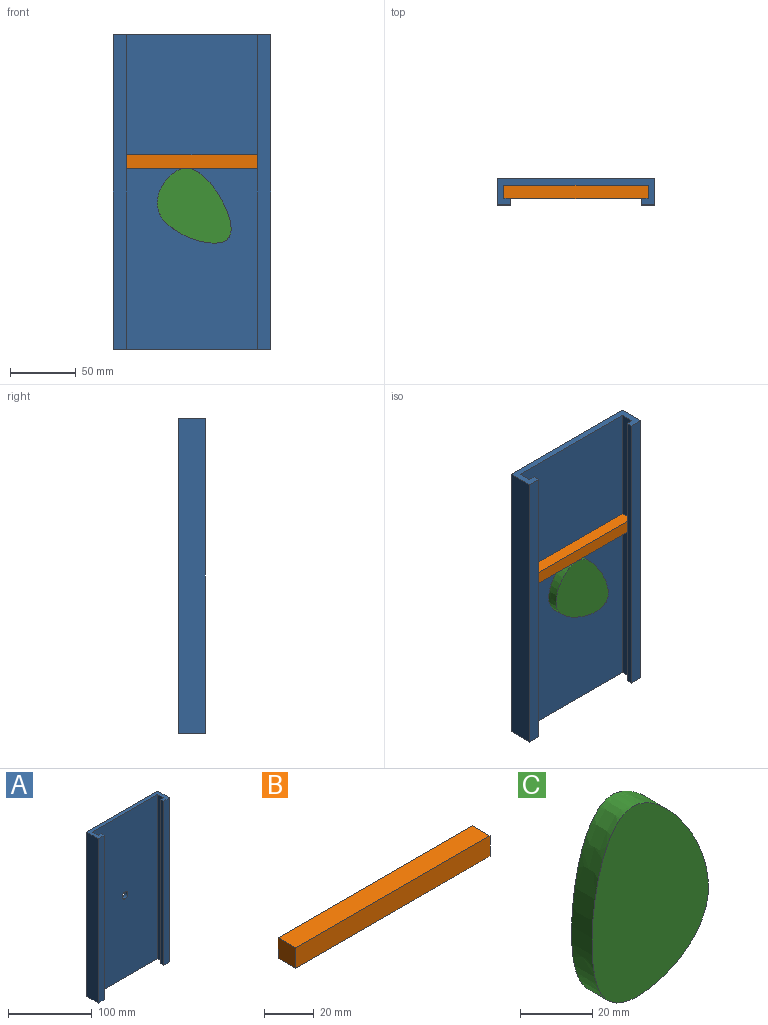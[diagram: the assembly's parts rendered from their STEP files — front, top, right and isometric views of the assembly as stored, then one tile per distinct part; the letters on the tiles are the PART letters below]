
ASSEMBLY  parts=3 mates=2
PART A: 15 faces, bbox 120x20x240 mm
  f0: plane 240x5mm, normal (1,0,0), area 1200mm2, adj f1,f3,f8,f13
  f1: plane 120x20mm, normal (0,0,-1), area 800mm2, adj f0,f2,f4,f5,f6,f7,f8,f9
  f2: plane 240x5mm, normal (-1,0,0), area 1200mm2, adj f1,f3,f6,f11
  f3: plane 120x20mm, normal (0,0,1), area 800mm2, adj f0,f2,f4,f5,f6,f7,f8,f9
  f4: plane 240x110mm, normal (0,-1,0), area 26321.5mm2, adj f1,f3,f5,f7,f14
  f5: plane 240x10mm, normal (-1,0,0), area 2400mm2, adj f1,f3,f4,f6
  f6: plane 240x5mm, normal (0,1,0), area 1200mm2, adj f1,f2,f3,f5
  f7: plane 240x10mm, normal (1,0,0), area 2400mm2, adj f1,f3,f4,f8
  f8: plane 240x5mm, normal (0,1,0), area 1200mm2, adj f0,f1,f3,f7
  f9: plane 240x120mm, normal (0,1,0), area 28721.5mm2, adj f1,f3,f10,f12,f14
  f10: plane 240x20mm, normal (1,0,0), area 4800mm2, adj f1,f3,f9,f11
  f11: plane 240x10mm, normal (0,-1,0), area 2400mm2, adj f1,f2,f3,f10
  f12: plane 240x20mm, normal (-1,0,0), area 4800mm2, adj f1,f3,f9,f13
  f13: plane 240x10mm, normal (0,-1,0), area 2400mm2, adj f0,f1,f3,f12
  f14: cylinder r=5mm len=10mm, axis (0,-1,0), area 157.1mm2, adj f4,f9
PART B: 6 faces, bbox 110x10x10 mm
  f0: plane 10x10mm, normal (1,0,0), area 100mm2, adj f1,f2,f4,f5
  f1: plane 110x10mm, normal (0,0,1), area 1100mm2, adj f0,f3,f4,f5
  f2: plane 110x10mm, normal (0,0,-1), area 1100mm2, adj f0,f3,f4,f5
  f3: plane 10x10mm, normal (-1,0,0), area 100mm2, adj f1,f2,f4,f5
  f4: plane 110x10mm, normal (0,1,0), area 1100mm2, adj f0,f1,f2,f3
  f5: plane 110x10mm, normal (0,-1,0), area 1100mm2, adj f0,f1,f2,f3
PART C: 5 faces, bbox 51x15x69 mm
  f0: plane 10x10mm, normal (0,1,0), area 78.5mm2, adj f1
  f1: cylinder r=5mm len=10mm, axis (0,-1,0), area 219.9mm2, adj f0,f4
  f2: extruded ~65.1x45.46mm, area 1405.8mm2, adj f3,f4
  f3: plane 69.02x51.05mm, normal (0,-1,0), area 2271.9mm2, adj f2
  f4: plane 69.02x51.05mm, normal (0,1,0), area 2193.4mm2, adj f1,f2
PLACE A t=(52.84,38.78,-107.09)mm fixed
PLACE B t=(52.84,38.78,-198.84)mm
PLACE C rot(axis=(0,1,0),143.4deg) t=(149.12,38.78,-35.46)mm
MATE slider A.f3 <-> B.f1  axis (0,0,1) through (-2.16,40.78,12.91)mm
MATE revolute A.f14 <-> C.f1  axis (0,1,0) through (52.84,45.78,-107.09)mm
